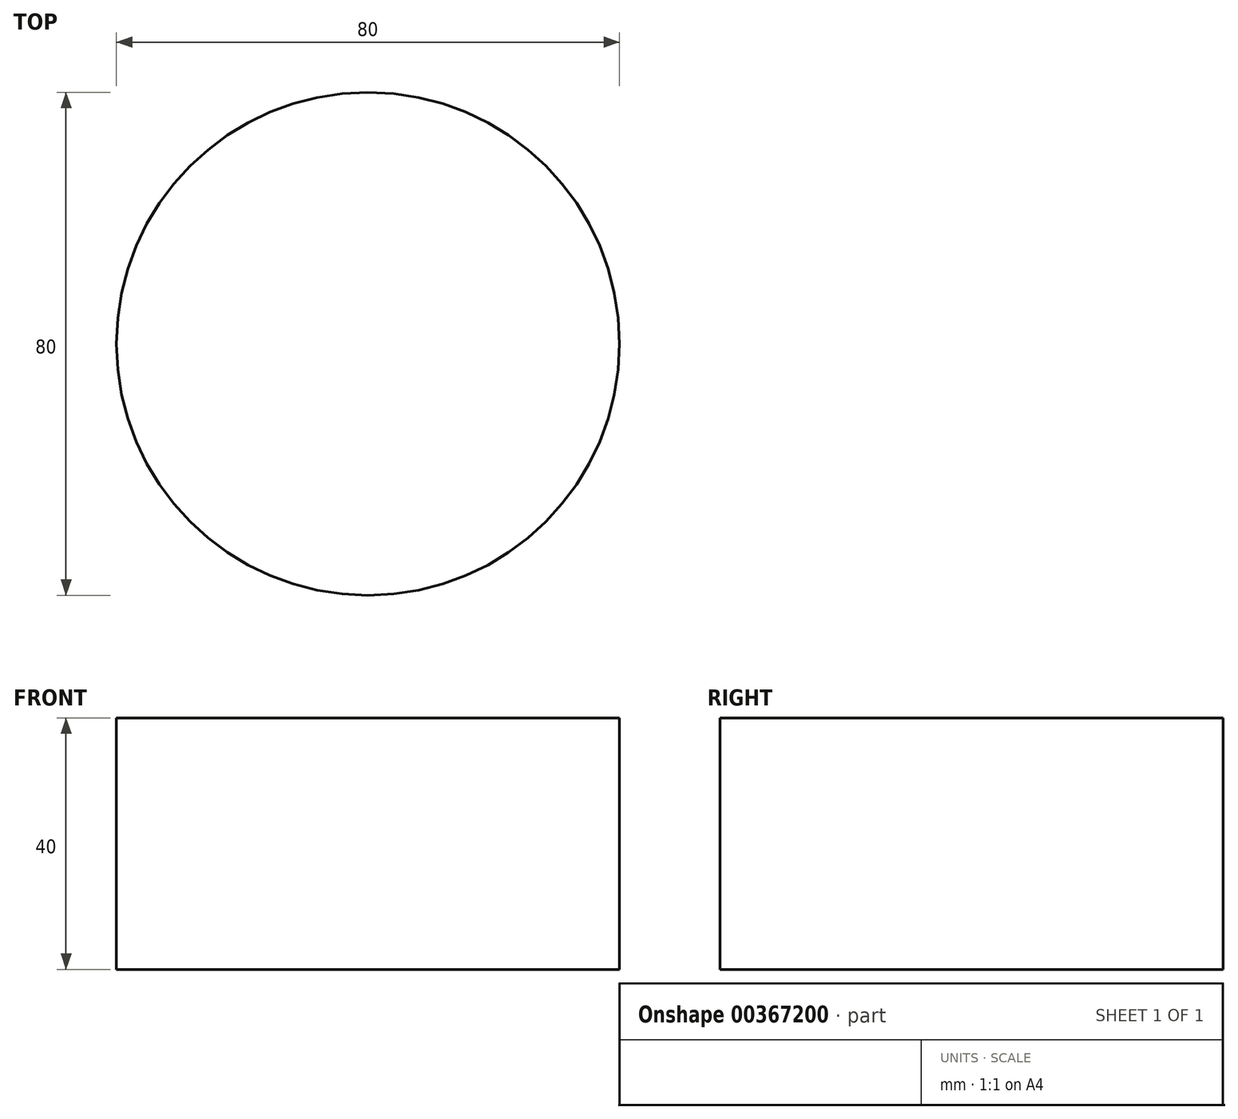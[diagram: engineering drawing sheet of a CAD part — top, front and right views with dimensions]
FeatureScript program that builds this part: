
annotation { "Feature Type Name" : "Feature", "Feature Type Description" : "" }
export const myFeature = defineFeature(function(context is Context, id is Id, definition is map)
    precondition{}
    {
        {
            var Q0;
            Q0=qCreatedBy(makeId("Front.planeOp"),FACE);
            var sketch = newSketch(context, id + "F0", { "sketchPlane" : qUnion([Q0])});
            skLineSegment(sketch, "E0.bottom", {"start": v(0, 0) * mm, "end": v(40, 0) * mm});
            skLineSegment(sketch, "E0.top", {"start": v(0, 40) * mm, "end": v(40, 40) * mm});
            skLineSegment(sketch, "E0.left", {"start": v(0, 0) * mm, "end": v(0, 40) * mm});
            skLineSegment(sketch, "E0.right", {"start": v(40, 0) * mm, "end": v(40, 40) * mm});
            skSolve(sketch);
        }
        {
            var Q0;
            Q0 = qSketchRegion(id + "F0", true);
            var Q1;
            Q1=sQuery(id+"F0.wireOp",EDGE,"E0.left");
            revolve(context, id + "F1", {"entities" : qUnion([Q0]), "axis" : qUnion([Q1]), "revolveType" : RevolveType.FULL});
        }
    });
